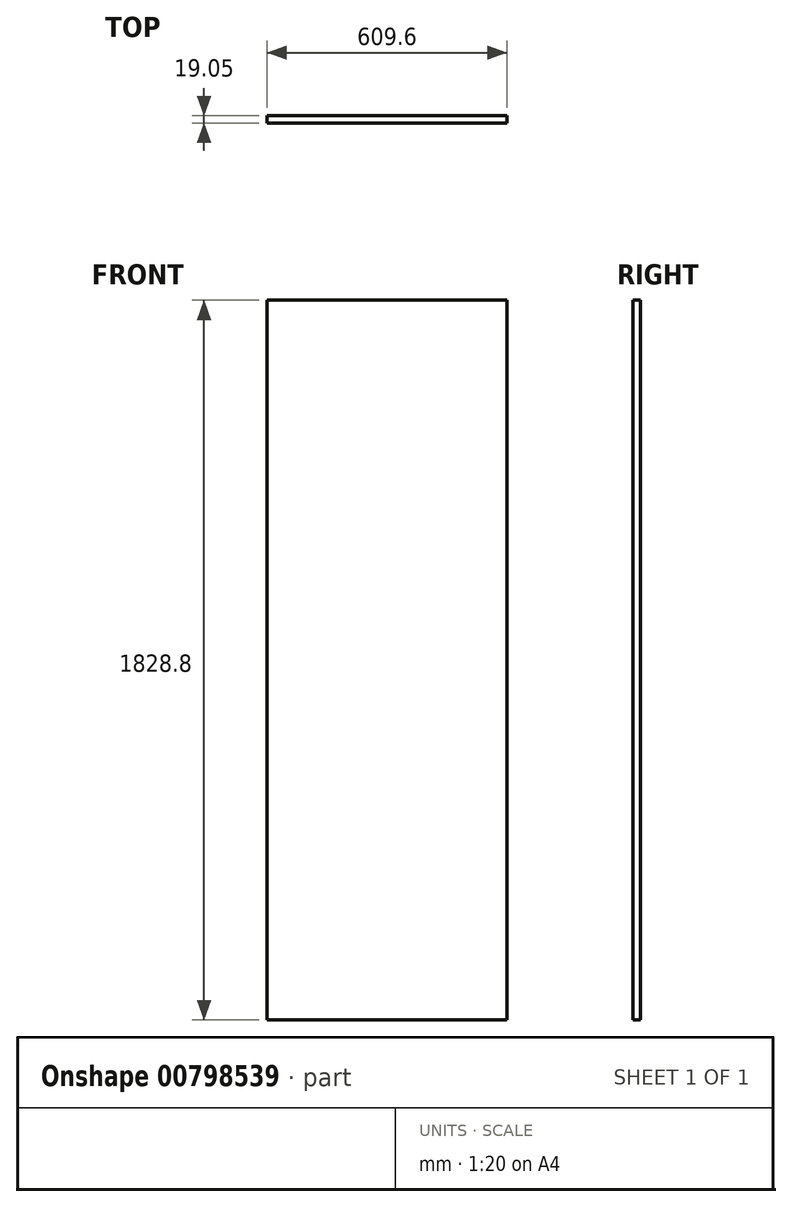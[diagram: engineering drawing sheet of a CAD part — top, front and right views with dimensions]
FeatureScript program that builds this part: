
annotation { "Feature Type Name" : "Feature", "Feature Type Description" : "" }
export const myFeature = defineFeature(function(context is Context, id is Id, definition is map)
    precondition{}
    {
        {
            var Q0;
            Q0=qCreatedBy(makeId("Front.planeOp"),FACE);
            var sketch = newSketch(context, id + "F0", { "sketchPlane" : qUnion([Q0])});
            skLineSegment(sketch, "E0.bottom", {"start": v(304.8, 914.4) * mm, "end": v(-304.8, 914.4) * mm});
            skLineSegment(sketch, "E0.top", {"start": v(304.8, -914.4) * mm, "end": v(-304.8, -914.4) * mm});
            skLineSegment(sketch, "E0.left", {"start": v(304.8, 914.4) * mm, "end": v(304.8, -914.4) * mm});
            skLineSegment(sketch, "E0.right", {"start": v(-304.8, 914.4) * mm, "end": v(-304.8, -914.4) * mm});
            skPoint(sketch, "E0.middle", {"position": v(0, 0) * mm});
            skSolve(sketch);
        }
        {
            var Q0;
            Q0 = qSketchRegion(id + "F0", true);
            extrude(context, id + "F1", {"entities" : qUnion([Q0]), "depth" : 19.05 * mm, "offsetDistance" : 30.48 * mm});
        }
    });
